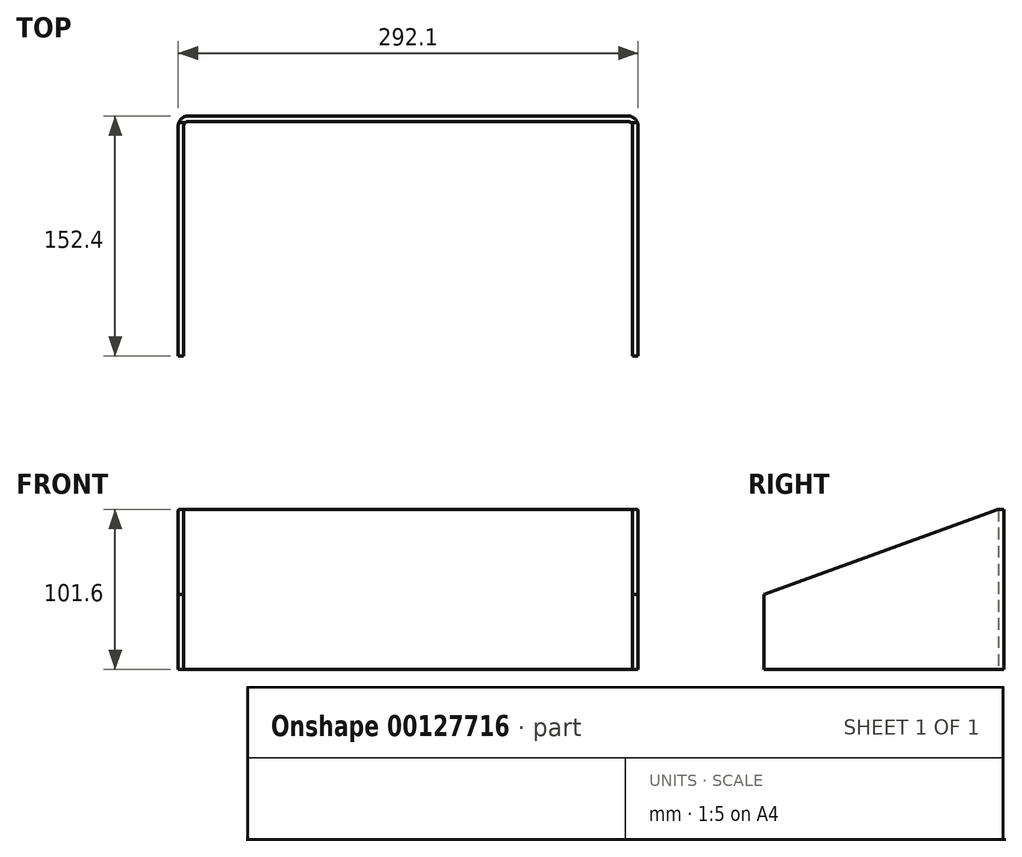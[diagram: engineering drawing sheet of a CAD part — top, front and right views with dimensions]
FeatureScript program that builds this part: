
annotation { "Feature Type Name" : "Feature", "Feature Type Description" : "" }
export const myFeature = defineFeature(function(context is Context, id is Id, definition is map)
    precondition{}
    {
        {
            var Q0;
            Q0=qCreatedBy(makeId("Top.planeOp"),FACE);
            var sketch = newSketch(context, id + "F0", { "sketchPlane" : qUnion([Q0])});
            skLineSegment(sketch, "E0.bottom", {"start": v(0, 0) * mm, "end": v(3.43, 0) * mm});
            skLineSegment(sketch, "E0.top", {"start": v(0, 152.4) * mm, "end": v(292.1, 152.4) * mm});
            skLineSegment(sketch, "E0.left", {"start": v(0, 0) * mm, "end": v(0, 152.4) * mm});
            skLineSegment(sketch, "E0.right", {"start": v(292.1, 0) * mm, "end": v(292.1, 152.4) * mm});
            skLineSegment(sketch, "E1", {"start": v(3.43, 148.97) * mm, "end": v(3.43, 0) * mm});
            skLineSegment(sketch, "E2", {"start": v(3.43, 148.97) * mm, "end": v(288.67, 148.97) * mm});
            skLineSegment(sketch, "E3", {"start": v(288.67, 148.97) * mm, "end": v(288.67, 0) * mm});
            skLineSegment(sketch, "E4.trimOffspring", {"start": v(288.67, 0) * mm, "end": v(292.1, 0) * mm});
            skSolve(sketch);
        }
        {
            var Q0;
            Q0 = qSketchRegion(id + "F0", true);
            extrude(context, id + "F1", {"entities" : qUnion([Q0]), "depth" : 101.6 * mm});
        }
        {
            var Q0;
            Q0=makeQuery(id+"F1.opExtrude","SWEPT_FACE",FACE,{"disambiguationData":[OSD([sQuery(id+"F0.wireOp",EDGE,"E0.right")])]});
            var sketch = newSketch(context, id + "F2", { "sketchPlane" : qUnion([Q0])});
            skLineSegment(sketch, "E5", {"start": v(0, 47.62) * mm, "end": v(183.19, 114.3) * mm});
            skLineSegment(sketch, "E6", {"start": v(183.19, 114.3) * mm, "end": v(0, 114.3) * mm});
            skLineSegment(sketch, "E7", {"start": v(0, 114.3) * mm, "end": v(0, 47.63) * mm});
            skSolve(sketch);
        }
        {
            var Q0;
            Q0=makeQuery(id+"F2.imprint","IMPRINT",FACE,{"disambiguationData":[TD([[makeQuery(id+"F2.imprint","IMPRINT",EDGE,{"derivedFrom":sQuery(id+"F2.wireOp",EDGE,"E5")}),1.0]])]});
            extrude(context, id + "F3", {"entities" : qUnion([Q0]), "operationType" : NewBodyOperationType.REMOVE, "endBound" : BoundingType.THROUGH_ALL, "oppositeDirection" : true, "depth" : 25.4 * mm});
        }
        {
            var Q0;
            Q0=makeQuery(id+"F1.opExtrude","SWEPT_EDGE",EDGE,{"disambiguationData":[OSD([sQuery(id+"F0.wireOp",EDGE,"E2"),sQuery(id+"F0.wireOp",EDGE,"E3")])]});
            var Q1;
            Q1=makeQuery(id+"F1.opExtrude","SWEPT_EDGE",EDGE,{"disambiguationData":[OSD([sQuery(id+"F0.wireOp",EDGE,"E1"),sQuery(id+"F0.wireOp",EDGE,"E2")])]});
            fillet(context, id + "F4", {"entities" : qUnion([Q0, Q1]), "radius" : 3.17 * mm, "tangentPropagation" : true, "allowEdgeOverflow" : false});
        }
        {
            var Q0;
            Q0=makeQuery(id+"F1.opExtrude","SWEPT_EDGE",EDGE,{"disambiguationData":[OSD([sQuery(id+"F0.wireOp",EDGE,"E0.top"),sQuery(id+"F0.wireOp",EDGE,"E0.left")])]});
            var Q1;
            Q1=makeQuery(id+"F1.opExtrude","SWEPT_EDGE",EDGE,{"disambiguationData":[OSD([sQuery(id+"F0.wireOp",EDGE,"E0.top"),sQuery(id+"F0.wireOp",EDGE,"E0.right")])]});
            fillet(context, id + "F5", {"entities" : qUnion([Q0, Q1]), "radius" : 6.35 * mm, "tangentPropagation" : true, "allowEdgeOverflow" : false});
        }
    });
